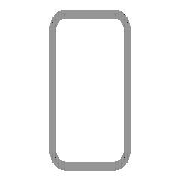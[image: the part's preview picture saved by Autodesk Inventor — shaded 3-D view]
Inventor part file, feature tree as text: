
AUTODESK INVENTOR PART (.ipt)
format: ipt  version: 2017 (Build 210142000, 142)  size: 126,976 bytes
history: native  units: mm (DEFAULTED — no unit token found)
features: other x4, sketch x3, plane x1
ambient origin geometry x8: Origin, YZ Plane, XZ Plane, XY Plane, X Axis, Y Axis, Z Axis, Center Point
bodies: Solid1 (feature_tree), Body (feature_tree)
feature tree (8):
  parser-record x1  (decoder bookkeeping rows leaked as tree rows — omitted from the tree; the rows remain in map.json)
  other  "Driven Length"
  other  "Start plane"
  other  "End plane"
  sketch  "Sketch"  dims[d10=203.2mm d11=76.2mm d12=6.35mm d13=-0.0mm d14=2438.4mm d15=101.6mm d16=38.1mm d17=12.7mm d18=90.0deg d19=2438.4mm]
  sketch  "Sketch3"  dims[d3=2438.4mm]
  plane  "Work Plane3"
  sketch  "Sketch4"  dims[d4=0.0mm]
